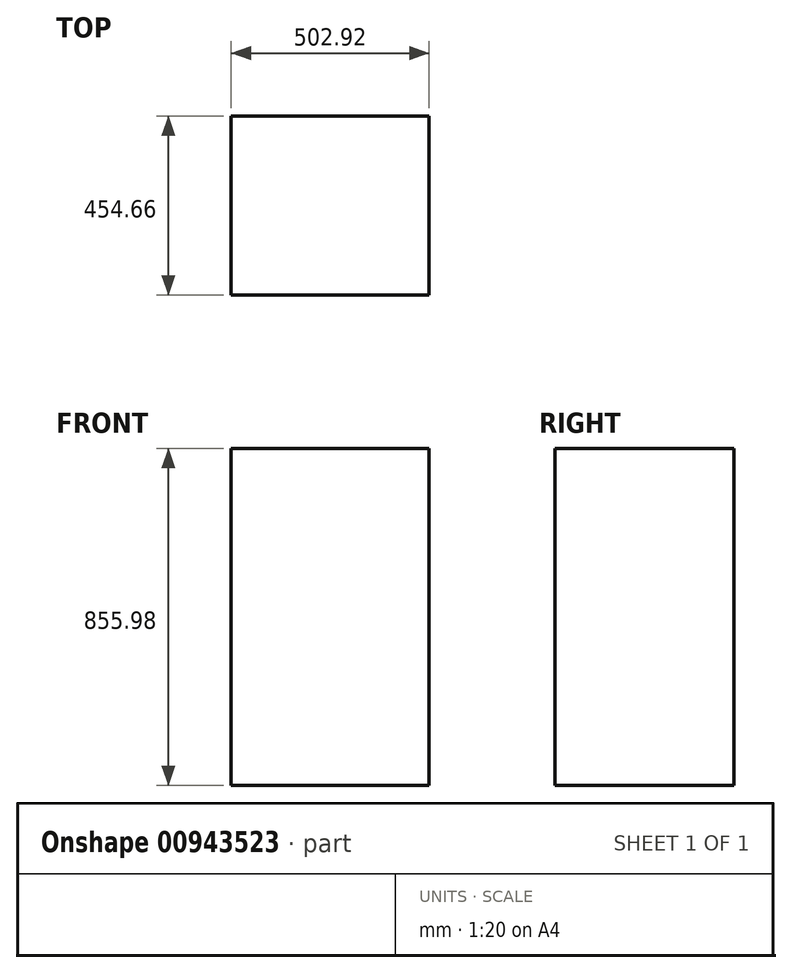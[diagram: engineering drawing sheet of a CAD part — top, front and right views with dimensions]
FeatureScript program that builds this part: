
annotation { "Feature Type Name" : "Feature", "Feature Type Description" : "" }
export const myFeature = defineFeature(function(context is Context, id is Id, definition is map)
    precondition{}
    {
        {
            var Q0;
            Q0=qCreatedBy(makeId("Front.planeOp"),FACE);
            var sketch = newSketch(context, id + "F0", { "sketchPlane" : qUnion([Q0])});
            skLineSegment(sketch, "E0.bottom", {"start": v(0, 0) * mm, "end": v(502.92, 0) * mm});
            skLineSegment(sketch, "E0.top", {"start": v(0, 855.98) * mm, "end": v(502.92, 855.98) * mm});
            skLineSegment(sketch, "E0.left", {"start": v(0, 0) * mm, "end": v(0, 855.98) * mm});
            skLineSegment(sketch, "E0.right", {"start": v(502.92, 0) * mm, "end": v(502.92, 855.98) * mm});
            skSolve(sketch);
        }
        {
            var Q0;
            Q0=makeQuery(id+"F0.imprint","IMPRINT",FACE,{"disambiguationData":[TD([[makeQuery(id+"F0.imprint","IMPRINT",EDGE,{"derivedFrom":sQuery(id+"F0.wireOp",EDGE,"E0.bottom")}),1.0]])]});
            extrude(context, id + "F1", {"entities" : qUnion([Q0]), "depth" : 454.66 * mm, "offsetDistance" : 25.4 * mm});
        }
    });
